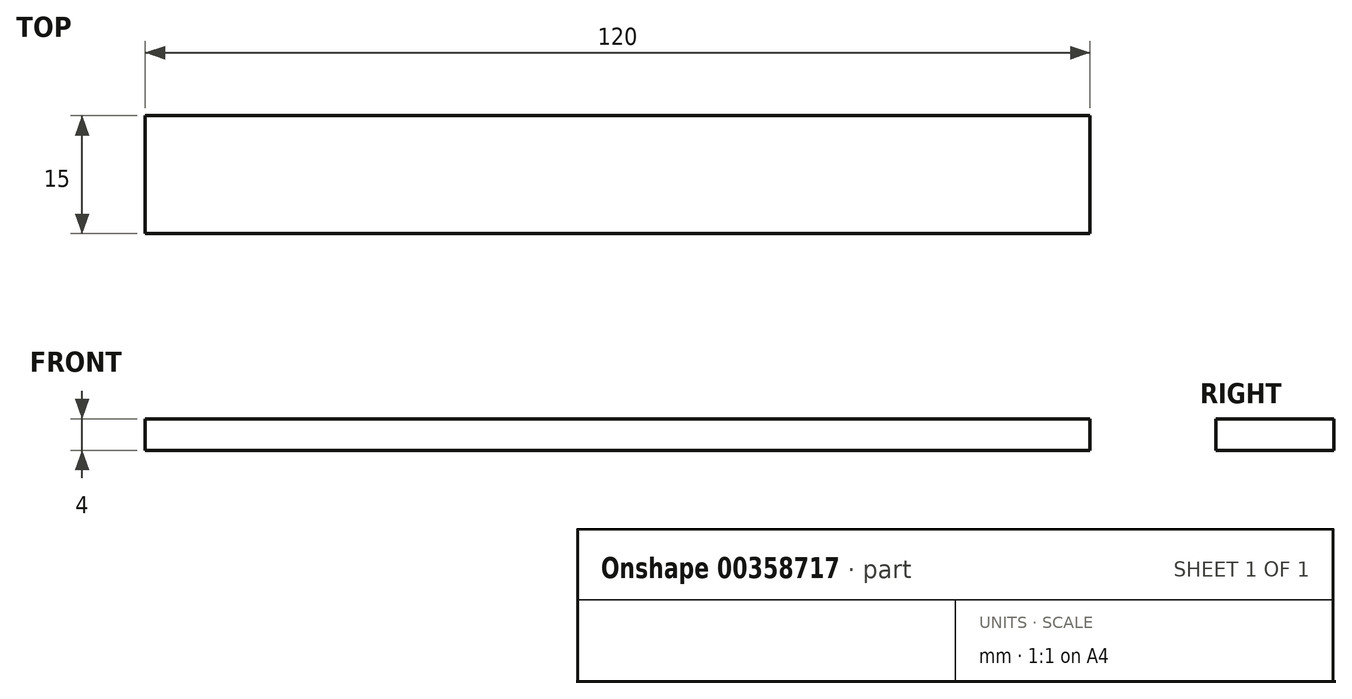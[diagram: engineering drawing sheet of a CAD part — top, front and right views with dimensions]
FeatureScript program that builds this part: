
annotation { "Feature Type Name" : "Feature", "Feature Type Description" : "" }
export const myFeature = defineFeature(function(context is Context, id is Id, definition is map)
    precondition{}
    {
        {
            var Q0;
            Q0=qCreatedBy(makeId("Right.planeOp"),FACE);
            var sketch = newSketch(context, id + "F0", { "sketchPlane" : qUnion([Q0])});
            skLineSegment(sketch, "E0.bottom", {"start": v(7.5, -2) * mm, "end": v(-7.5, -2) * mm});
            skLineSegment(sketch, "E0.top", {"start": v(7.5, 2) * mm, "end": v(-7.5, 2) * mm});
            skLineSegment(sketch, "E0.left", {"start": v(7.5, -2) * mm, "end": v(7.5, 2) * mm});
            skLineSegment(sketch, "E0.right", {"start": v(-7.5, -2) * mm, "end": v(-7.5, 2) * mm});
            skPoint(sketch, "E0.middle", {"position": v(0, 0) * mm});
            skSolve(sketch);
        }
        {
            var Q0;
            Q0 = qSketchRegion(id + "F0", true);
            extrude(context, id + "F1", {"entities" : qUnion([Q0]), "depth" : 120 * mm});
        }
    });
